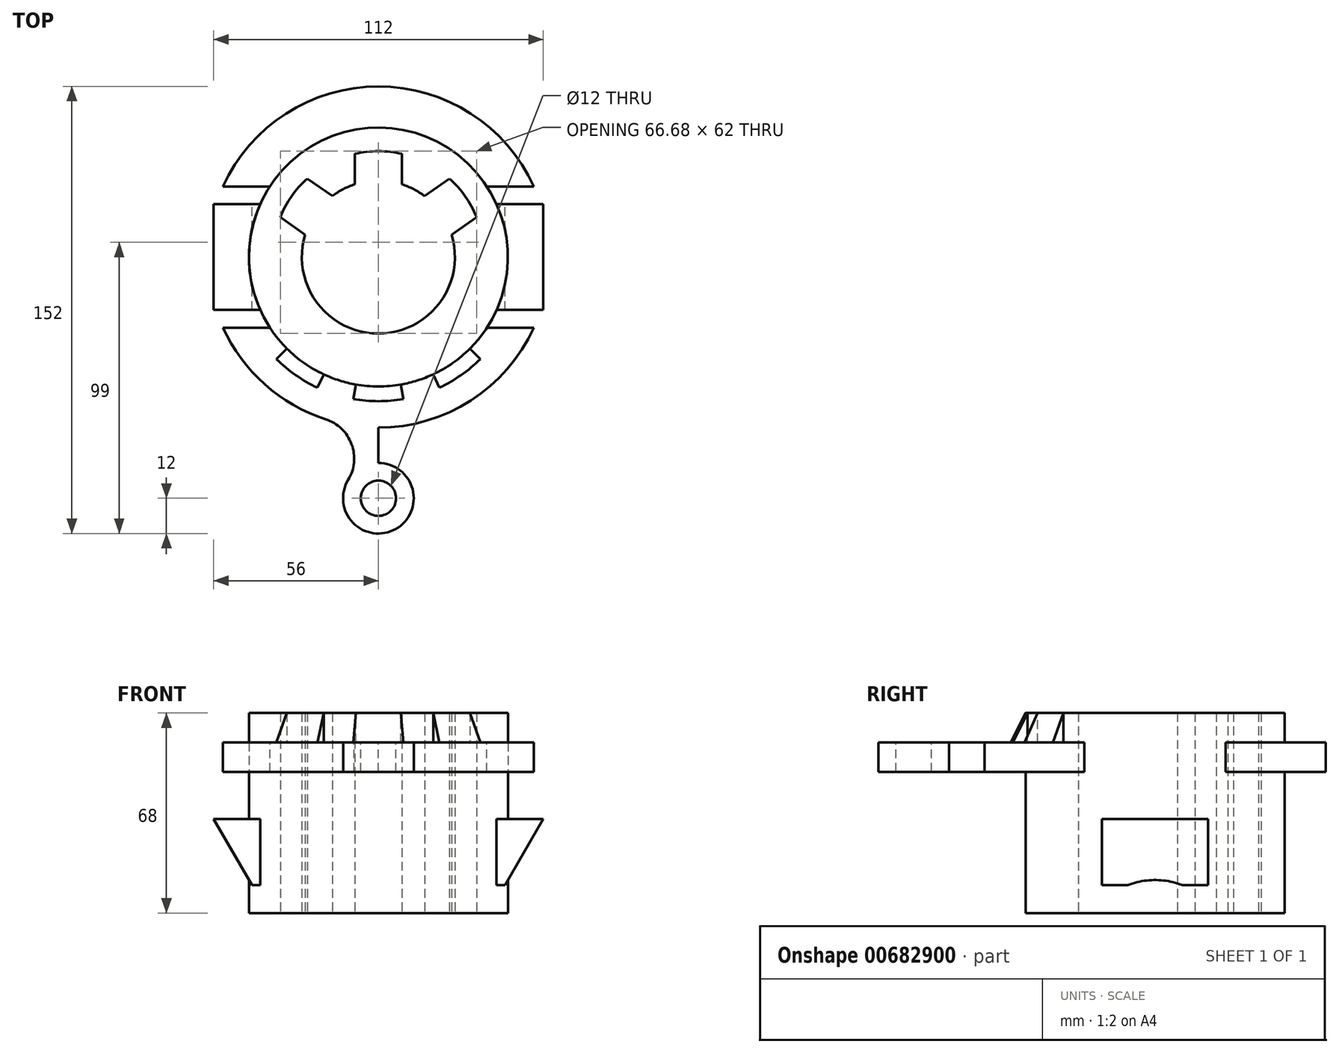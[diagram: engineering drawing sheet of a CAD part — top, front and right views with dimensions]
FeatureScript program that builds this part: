
annotation { "Feature Type Name" : "Feature", "Feature Type Description" : "" }
export const myFeature = defineFeature(function(context is Context, id is Id, definition is map)
    precondition{}
    {
        {
            var Q0;
            Q0=qCreatedBy(makeId("Top.planeOp"),FACE);
            var sketch = newSketch(context, id + "F0", { "sketchPlane" : qUnion([Q0])});
            skArc(sketch, "E0", {"start": v(-8, 24.74) * mm, "mid": v(-12, 23.06) * mm, "end": v(-15.68, 20.74) * mm});
            skCircle(sketch, "E1", {"center": v(0, 0) * mm, "radius": 44 * mm});
            skCircle(sketch, "E2", {"center": v(0, 0) * mm, "radius": 36 * mm});
            skLineSegment(sketch, "E3", {"start": v(0, 36) * mm, "end": v(0, 26) * mm});
            skLineSegment(sketch, "E4.0", {"start": v(8, 35.1) * mm, "end": v(8, 24.74) * mm});
            skLineSegment(sketch, "E5", {"start": v(0, 0) * mm, "end": v(41.6, 29.13) * mm});
            skLineSegment(sketch, "E6.MirrorCS", {"start": v(-8, 35.1) * mm, "end": v(-8, 24.74) * mm});
            skLineSegment(sketch, "E7", {"start": v(0, 0) * mm, "end": v(21.24, 40.8) * mm});
            skLineSegment(sketch, "E8.MirrorCS", {"start": v(24.16, 26.69) * mm, "end": v(15.68, 20.74) * mm});
            skLineSegment(sketch, "E9.MirrorCS", {"start": v(33.34, 13.58) * mm, "end": v(24.85, 7.64) * mm});
            skLineSegment(sketch, "E10.MirrorCS", {"start": v(-24.16, 26.69) * mm, "end": v(-15.68, 20.74) * mm});
            skLineSegment(sketch, "E11.MirrorCS", {"start": v(-33.34, 13.58) * mm, "end": v(-24.85, 7.64) * mm});
            skArc(sketch, "E12.trimOffspring", {"start": v(-24.85, 7.64) * mm, "mid": v(0, -26) * mm, "end": v(24.85, 7.64) * mm});
            skArc(sketch, "E13.trimOffspring", {"start": v(15.68, 20.74) * mm, "mid": v(12, 23.06) * mm, "end": v(8, 24.74) * mm});
            skSolve(sketch);
        }
        {
            var Q0;
            Q0=makeQuery(id+"F0.imprint","IMPRINT",FACE,{"disambiguationData":[TD([[makeQuery(id+"F0.imprint","IMPRINT",EDGE,{"derivedFrom":sQuery(id+"F0.wireOp",EDGE,"E0")}),-1.0]])]});
            var Q1;
            {var subQ0=sQuery(id+"F0.wireOp",EDGE,"E9.MirrorCS");Q1=makeQuery(id+"F0.imprint","IMPRINT",FACE,{"disambiguationData":[TD([[makeQuery(id+"F0.imprint","IMPRINT",EDGE,{"derivedFrom":subQ0}),1.0]])]});}
            var Q2;
            {var subQ0=sQuery(id+"F0.wireOp",EDGE,"E8.MirrorCS");Q2=makeQuery(id+"F0.imprint","IMPRINT",FACE,{"disambiguationData":[TD([[makeQuery(id+"F0.imprint","IMPRINT",EDGE,{"derivedFrom":subQ0}),-1.0]])]});}
            var Q3;
            {var subQ0=sQuery(id+"F0.wireOp",EDGE,"E4.0");Q3=makeQuery(id+"F0.imprint","IMPRINT",FACE,{"disambiguationData":[TD([[makeQuery(id+"F0.imprint","IMPRINT",EDGE,{"derivedFrom":subQ0}),1.0]])]});}
            var Q4;
            {var subQ0=sQuery(id+"F0.wireOp",EDGE,"E2");var subQ9=makeQuery(id+"F0.imprint","IMPRINT",VERTEX,{"derivedFrom":subQ0});Q4=makeQuery(id+"F0.imprint","IMPRINT",FACE,{"disambiguationData":[TD([[makeQuery(id+"F0.imprint","IMPRINT",EDGE,{"disambiguationData":[TD([[subQ9,1.0]])],"derivedFrom":subQ0}),-1.0]])]});}
            var Q5;
            {var subQ4=sQuery(id+"F0.wireOp",EDGE,"E5");var subQ5=sQuery(id+"F0.wireOp",EDGE,"E1");var subQ6=makeQuery(id+"F0.imprint","INTERSECT",VERTEX,{"derivedFrom":[subQ5,subQ4]});Q5=makeQuery(id+"F0.imprint","IMPRINT",FACE,{"disambiguationData":[TD([[makeQuery(id+"F0.imprint","IMPRINT",EDGE,{"disambiguationData":[TD([[subQ6,-1.0]])],"derivedFrom":subQ5}),1.0]])]});}
            extrude(context, id + "F1", {"entities" : qUnion([Q0, Q1, Q2, Q3, Q4, Q5]), "depth" : 68 * mm, "offsetDistance" : 25 * mm});
        }
        {
            var Q0;
            Q0=qCreatedBy(makeId("Right.planeOp"),FACE);
            var sketch = newSketch(context, id + "F2", { "sketchPlane" : qUnion([Q0])});
            skLineSegment(sketch, "E14", {"start": v(0, 0) * mm, "end": v(0, 68) * mm});
            skLineSegment(sketch, "E15", {"start": v(0, 68) * mm, "end": v(-44, 68) * mm});
            skLineSegment(sketch, "E16", {"start": v(-44, 68) * mm, "end": v(-44, 58) * mm});
            skLineSegment(sketch, "E17", {"start": v(-44, 58) * mm, "end": v(-49, 58) * mm});
            skLineSegment(sketch, "E18", {"start": v(-49, 58) * mm, "end": v(-44, 68) * mm});
            skSolve(sketch);
        }
        {
            var Q0;
            Q0=makeQuery(id+"F2.imprint","IMPRINT",FACE,{"disambiguationData":[TD([[makeQuery(id+"F2.imprint","IMPRINT",EDGE,{"derivedFrom":sQuery(id+"F2.wireOp",EDGE,"E16")}),-1.0]])]});
            var Q1;
            Q1=sQuery(id+"F2.wireOp",EDGE,"E14");
            revolve(context, id + "F3", {"operationType" : NewBodyOperationType.ADD, "entities" : qUnion([Q0]), "axis" : qUnion([Q1]), "revolveType" : RevolveType.SYMMETRIC, "angle" : 90 * degree});
        }
        {
            var Q0;
            Q0=makeQuery(id+"F1.opExtrude","CAP_FACE",FACE,{"disambiguationData":[OSD([sQuery(id+"F0.wireOp",EDGE,"E0"),sQuery(id+"F0.wireOp",EDGE,"E1"),sQuery(id+"F0.wireOp",EDGE,"E2"),sQuery(id+"F0.wireOp",EDGE,"E4.0"),sQuery(id+"F0.wireOp",EDGE,"E6.MirrorCS"),sQuery(id+"F0.wireOp",EDGE,"E8.MirrorCS"),sQuery(id+"F0.wireOp",EDGE,"E9.MirrorCS"),sQuery(id+"F0.wireOp",EDGE,"E10.MirrorCS"),sQuery(id+"F0.wireOp",EDGE,"E11.MirrorCS"),sQuery(id+"F0.wireOp",EDGE,"E12.trimOffspring"),sQuery(id+"F0.wireOp",EDGE,"E13.trimOffspring")])],"isStart":false});
            var sketch = newSketch(context, id + "F4", { "sketchPlane" : qUnion([Q0])});
            skLineSegment(sketch, "E19", {"start": v(0, 0) * mm, "end": v(0, -49) * mm});
            skLineSegment(sketch, "E20", {"start": v(0, 0) * mm, "end": v(-28.1, -40.14) * mm});
            skLineSegment(sketch, "E21", {"start": v(0, 0) * mm, "end": v(-34.65, -34.65) * mm});
            skCircle(sketch, "E22", {"center": v(0, 0) * mm, "radius": 44 * mm});
            skLineSegment(sketch, "E23", {"start": v(0, 0) * mm, "end": v(-8.5, -48.26) * mm});
            skLineSegment(sketch, "E24", {"start": v(0, 0) * mm, "end": v(8.5, -48.26) * mm});
            skLineSegment(sketch, "E25", {"start": v(0, 0) * mm, "end": v(20.7, -44.4) * mm});
            skCircle(sketch, "E26", {"center": v(0, 0) * mm, "radius": 49 * mm});
            skLineSegment(sketch, "E27.MirrorCS", {"start": v(0, 0) * mm, "end": v(-20.7, -44.4) * mm});
            skSolve(sketch);
        }
        {
            var Q0;
            {var subQ0=sQuery(id+"F4.wireOp",EDGE,"E27.MirrorCS");var subQ1=sQuery(id+"F4.wireOp",EDGE,"E22");var subQ2=makeQuery(id+"F4.imprint","INTERSECT",VERTEX,{"derivedFrom":[subQ1,subQ0]});Q0=makeQuery(id+"F4.imprint","IMPRINT",FACE,{"disambiguationData":[TD([[makeQuery(id+"F4.imprint","IMPRINT",EDGE,{"disambiguationData":[TD([[subQ2,-1.0]])],"derivedFrom":subQ1}),-1.0]])]});}
            var Q1;
            {var subQ0=sQuery(id+"F4.wireOp",EDGE,"E24");var subQ1=sQuery(id+"F4.wireOp",EDGE,"E22");var subQ2=makeQuery(id+"F4.imprint","INTERSECT",VERTEX,{"derivedFrom":[subQ1,subQ0]});Q1=makeQuery(id+"F4.imprint","IMPRINT",FACE,{"disambiguationData":[TD([[makeQuery(id+"F4.imprint","IMPRINT",EDGE,{"disambiguationData":[TD([[subQ2,-1.0]])],"derivedFrom":subQ1}),-1.0]])]});}
            var Q2;
            Q2=makeQuery(id+"F3.opRevolve","SWEPT_FACE",FACE,{"disambiguationData":[OSD([sQuery(id+"F2.wireOp",EDGE,"E17")])]});
            extrude(context, id + "F5", {"entities" : qUnion([Q0, Q1]), "operationType" : NewBodyOperationType.REMOVE, "endBound" : BoundingType.UP_TO_SURFACE, "oppositeDirection" : true, "depth" : 25 * mm, "endBoundEntityFace" : qUnion([Q2]), "offsetDistance" : 25 * mm});
        }
        {
            var Q0;
            {var subQ2=sQuery(id+"F4.wireOp",EDGE,"E23");Q0=makeQuery(id+"F5.boolean.opBoolean","SPLIT",FACE,{"disambiguationData":[TD([makeQuery(id+"F5.opExtrude","SWEPT_FACE",FACE,{"disambiguationData":[OSD([subQ2])]})])],"derivedFrom":makeQuery(id+"F3.opRevolve","SWEPT_FACE",FACE,{"disambiguationData":[OSD([sQuery(id+"F2.wireOp",EDGE,"E17")])]})});}
            var sketch = newSketch(context, id + "F6", { "sketchPlane" : qUnion([Q0])});
            skCircle(sketch, "E28", {"center": v(0, 0) * mm, "radius": 44 * mm});
            skArc(sketch, "E29", {"start": v(-52.8, -24) * mm, "mid": v(0, -58) * mm, "end": v(52.8, -24) * mm});
            skLineSegment(sketch, "E30", {"start": v(-58, 0) * mm, "end": v(58, 0) * mm});
            skLineSegment(sketch, "E31.0", {"start": v(-58, -24) * mm, "end": v(58, -24) * mm});
            skLineSegment(sketch, "E32.MirrorCS", {"start": v(-58, 24) * mm, "end": v(58, 24) * mm});
            skArc(sketch, "E33.trimOffspring", {"start": v(52.8, 24) * mm, "mid": v(0, 58) * mm, "end": v(-52.8, 24) * mm});
            skLineSegment(sketch, "E34", {"start": v(0, 0) * mm, "end": v(0, 82) * mm});
            skCircle(sketch, "E35", {"center": v(0, 82) * mm, "radius": 6 * mm});
            skCircle(sketch, "E36", {"center": v(0, 82) * mm, "radius": 12 * mm});
            skArc(sketch, "E37", {"start": v(-17.9, 55.17) * mm, "mid": v(-9.09, 63.62) * mm, "end": v(-10.25, 75.76) * mm});
            skArc(sketch, "E38.MirrorCS", {"start": v(17.9, 55.17) * mm, "mid": v(9.09, 63.62) * mm, "end": v(10.25, 75.76) * mm});
            skSolve(sketch);
        }
        {
            var Q0;
            {var subQ0=sQuery(id+"F6.wireOp",EDGE,"E33.trimOffspring");Q0=makeQuery(id+"F6.imprint","IMPRINT",FACE,{"disambiguationData":[TD([[makeQuery(id+"F6.imprint","IMPRINT",EDGE,{"derivedFrom":subQ0}),1.0]])]});}
            var Q1;
            {var subQ4=sQuery(id+"F6.wireOp",EDGE,"E29");Q1=makeQuery(id+"F6.imprint","IMPRINT",FACE,{"disambiguationData":[TD([[makeQuery(id+"F6.imprint","IMPRINT",EDGE,{"derivedFrom":subQ4}),1.0]])]});}
            var Q2;
            {var subQ1=sQuery(id+"F4.wireOp",EDGE,"E23");var subQ2=makeQuery(id+"F5.boolean.opBoolean","COPY",EDGE,{"derivedFrom":makeQuery(id+"F5.opExtrude","CAP_EDGE",EDGE,{"disambiguationData":[OSD([subQ1])],"isStart":false})});Q2=makeQuery(id+"F6.imprint","IMPRINT",FACE,{"disambiguationData":[TD([[makeQuery(id+"F6.imprint","IMPRINT",EDGE,{"derivedFrom":subQ2}),-1.0]])]});}
            var Q3;
            {var subQ1=sQuery(id+"F4.wireOp",EDGE,"E24");var subQ2=makeQuery(id+"F5.boolean.opBoolean","COPY",EDGE,{"derivedFrom":makeQuery(id+"F5.opExtrude","CAP_EDGE",EDGE,{"disambiguationData":[OSD([subQ1])],"isStart":false})});Q3=makeQuery(id+"F6.imprint","IMPRINT",FACE,{"disambiguationData":[TD([[makeQuery(id+"F6.imprint","IMPRINT",EDGE,{"derivedFrom":subQ2}),1.0]])]});}
            var Q4;
            {var subQ0=sQuery(id+"F6.wireOp",EDGE,"E38.MirrorCS");Q4=makeQuery(id+"F6.imprint","IMPRINT",FACE,{"disambiguationData":[TD([[makeQuery(id+"F6.imprint","IMPRINT",EDGE,{"derivedFrom":subQ0}),1.0]])]});}
            var Q5;
            {var subQ0=sQuery(id+"F6.wireOp",EDGE,"E37");Q5=makeQuery(id+"F6.imprint","IMPRINT",FACE,{"disambiguationData":[TD([[makeQuery(id+"F6.imprint","IMPRINT",EDGE,{"derivedFrom":subQ0}),-1.0]])]});}
            var Q6;
            Q6=makeQuery(id+"F6.imprint","IMPRINT",FACE,{"disambiguationData":[TD([[makeQuery(id+"F6.imprint","IMPRINT",EDGE,{"derivedFrom":sQuery(id+"F6.wireOp",EDGE,"E35")}),-1.0]])]});
            extrude(context, id + "F7", {"entities" : qUnion([Q0, Q1, Q2, Q3, Q4, Q5, Q6]), "operationType" : NewBodyOperationType.ADD, "depth" : 10 * mm, "offsetDistance" : 25 * mm});
        }
        {
            var Q0;
            Q0=qCreatedBy(makeId("Front.planeOp"),FACE);
            var sketch = newSketch(context, id + "F8", { "sketchPlane" : qUnion([Q0])});
            skLineSegment(sketch, "E39", {"start": v(0, 0) * mm, "end": v(44, 0) * mm});
            skLineSegment(sketch, "E40", {"start": v(44, 0) * mm, "end": v(44, 32) * mm});
            skLineSegment(sketch, "E41", {"start": v(44, 32) * mm, "end": v(56, 32) * mm});
            skLineSegment(sketch, "E42", {"start": v(56, 32) * mm, "end": v(43, 9.48) * mm});
            skLineSegment(sketch, "E43", {"start": v(56, 32) * mm, "end": v(66.19, 32) * mm});
            skLineSegment(sketch, "E44", {"start": v(44, 32) * mm, "end": v(43, 32) * mm});
            skLineSegment(sketch, "E45", {"start": v(43, 32) * mm, "end": v(43, 9.48) * mm});
            skSolve(sketch);
        }
        {
            var Q0;
            {var subQ0=sQuery(id+"F8.wireOp",EDGE,"E44");Q0=makeQuery(id+"F8.imprint","IMPRINT",FACE,{"disambiguationData":[TD([[makeQuery(id+"F8.imprint","IMPRINT",EDGE,{"derivedFrom":subQ0}),1.0]])]});}
            var Q1;
            {var subQ0=sQuery(id+"F8.wireOp",EDGE,"E41");Q1=makeQuery(id+"F8.imprint","IMPRINT",FACE,{"disambiguationData":[TD([[makeQuery(id+"F8.imprint","IMPRINT",EDGE,{"derivedFrom":subQ0}),-1.0]])]});}
            extrude(context, id + "F9", {"entities" : qUnion([Q0, Q1]), "operationType" : NewBodyOperationType.ADD, "endBound" : BoundingType.SYMMETRIC, "depth" : 36 * mm, "offsetDistance" : 25 * mm});
        }
        {
            var Q0;
            {var subQ0=sQuery(id+"F8.wireOp",EDGE,"E45");var subQ1=sQuery(id+"F8.wireOp",EDGE,"E44");var subQ2=sQuery(id+"F8.wireOp",EDGE,"E42");var subQ3=sQuery(id+"F8.wireOp",EDGE,"E41");Q0=makeQuery(id+"F9.boolean.opBoolean","SPLIT",FACE,{"disambiguationData":[TD([makeQuery(id+"F9.opExtrude","CAP_FACE",FACE,{"disambiguationData":[OSD([subQ3,subQ2,subQ1,subQ0])],"isStart":true})])],"derivedFrom":makeQuery(id+"F9.opExtrude","SWEPT_FACE",FACE,{"disambiguationData":[OSD([subQ0])]})});}
            var Q1;
            {var subQ0=sQuery(id+"F8.wireOp",EDGE,"E45");var subQ1=sQuery(id+"F8.wireOp",EDGE,"E44");var subQ2=sQuery(id+"F8.wireOp",EDGE,"E42");var subQ3=sQuery(id+"F8.wireOp",EDGE,"E41");Q1=makeQuery(id+"F9.boolean.opBoolean","SPLIT",FACE,{"disambiguationData":[TD([makeQuery(id+"F9.opExtrude","CAP_FACE",FACE,{"disambiguationData":[OSD([subQ3,subQ2,subQ1,subQ0])],"isStart":false})])],"derivedFrom":makeQuery(id+"F9.opExtrude","SWEPT_FACE",FACE,{"disambiguationData":[OSD([subQ0])]})});}
            var Q2;
            {var subQ0=sQuery(id+"F6.wireOp",EDGE,"E31.0");var subQ1=sQuery(id+"F6.wireOp",EDGE,"E29");var subQ19=sQuery(id+"F0.wireOp",EDGE,"E1");var subQ23=sQuery(id+"F4.wireOp",EDGE,"E22");Q2=makeQuery(id+"F7.boolean.opBoolean","SPLIT",FACE,{"disambiguationData":[TD([makeQuery(id+"F7.opExtrude","SWEPT_FACE",FACE,{"disambiguationData":[OSD([subQ0]),TDD([makeQuery(id+"F6.imprint","IMPRINT",EDGE,{"disambiguationData":[TD([[makeQuery(id+"F6.imprint","INTERSECT",VERTEX,{"disambiguationData":[OD(0.0)],"derivedFrom":[subQ1,subQ0]}),-1.0]])],"derivedFrom":subQ0})])]})])],"derivedFrom":makeQuery(id+"F5.boolean.opBoolean","MERGE",FACE,{"derivedFrom":[makeQuery(id+"F1.opExtrude","SWEPT_FACE",FACE,{"disambiguationData":[OSD([subQ19])]})],"fromTools":[makeQuery(id+"F5.opExtrude","SWEPT_FACE",FACE,{"disambiguationData":[OSD([subQ23]),TDD([makeQuery(id+"F4.imprint","IMPRINT",EDGE,{"disambiguationData":[TD([[makeQuery(id+"F4.imprint","INTERSECT",VERTEX,{"derivedFrom":[subQ23,sQuery(id+"F4.wireOp",EDGE,"E27.MirrorCS")]}),-1.0]])],"derivedFrom":subQ23})])]}),makeQuery(id+"F5.opExtrude","SWEPT_FACE",FACE,{"disambiguationData":[OSD([subQ23]),TDD([makeQuery(id+"F4.imprint","IMPRINT",EDGE,{"disambiguationData":[TD([[makeQuery(id+"F4.imprint","INTERSECT",VERTEX,{"derivedFrom":[subQ23,sQuery(id+"F4.wireOp",EDGE,"E24")]}),-1.0]])],"derivedFrom":subQ23})])]})]})});}
            extrude(context, id + "F10", {"entities" : qUnion([Q0, Q1]), "operationType" : NewBodyOperationType.ADD, "endBound" : BoundingType.UP_TO_SURFACE, "depth" : 25 * mm, "endBoundEntityFace" : qUnion([Q2]), "offsetDistance" : 25 * mm});
        }
        {
            var Q0;
            Q0=qCreatedBy(makeId("Front.planeOp"),FACE);
            var sketch = newSketch(context, id + "F11", { "sketchPlane" : qUnion([Q0])});
            skLineSegment(sketch, "E46", {"start": v(0, 0) * mm, "end": v(-44, 0) * mm});
            skLineSegment(sketch, "E47", {"start": v(-44, 0) * mm, "end": v(-44, 32) * mm});
            skLineSegment(sketch, "E48", {"start": v(-44, 32) * mm, "end": v(-56, 32) * mm});
            skLineSegment(sketch, "E49", {"start": v(-44, 32) * mm, "end": v(-43, 32) * mm});
            skLineSegment(sketch, "E50", {"start": v(-56, 32) * mm, "end": v(-43, 9.48) * mm});
            skLineSegment(sketch, "E51", {"start": v(-43, 32) * mm, "end": v(-43, 9.48) * mm});
            skSolve(sketch);
        }
        {
            var Q0;
            {var subQ0=sQuery(id+"F11.wireOp",EDGE,"E48");Q0=makeQuery(id+"F11.imprint","IMPRINT",FACE,{"disambiguationData":[TD([[makeQuery(id+"F11.imprint","IMPRINT",EDGE,{"derivedFrom":subQ0}),1.0]])]});}
            var Q1;
            {var subQ0=sQuery(id+"F11.wireOp",EDGE,"E49");Q1=makeQuery(id+"F11.imprint","IMPRINT",FACE,{"disambiguationData":[TD([[makeQuery(id+"F11.imprint","IMPRINT",EDGE,{"derivedFrom":subQ0}),-1.0]])]});}
            extrude(context, id + "F12", {"entities" : qUnion([Q0, Q1]), "operationType" : NewBodyOperationType.ADD, "endBound" : BoundingType.SYMMETRIC, "depth" : 36 * mm, "offsetDistance" : 25 * mm});
        }
        {
            var Q0;
            {var subQ0=sQuery(id+"F11.wireOp",EDGE,"E49");var subQ1=sQuery(id+"F11.wireOp",EDGE,"E48");var subQ3=sQuery(id+"F11.wireOp",EDGE,"E51");var subQ4=sQuery(id+"F11.wireOp",EDGE,"E50");Q0=makeQuery(id+"F12.boolean.opBoolean","SPLIT",FACE,{"disambiguationData":[TD([makeQuery(id+"F12.opExtrude","CAP_FACE",FACE,{"disambiguationData":[OSD([subQ1,subQ0,subQ4,subQ3])],"isStart":false})])],"derivedFrom":makeQuery(id+"F12.opExtrude","SWEPT_FACE",FACE,{"disambiguationData":[OSD([subQ3])]})});}
            var Q1;
            {var subQ0=sQuery(id+"F11.wireOp",EDGE,"E49");var subQ1=sQuery(id+"F11.wireOp",EDGE,"E48");var subQ3=sQuery(id+"F11.wireOp",EDGE,"E51");var subQ4=sQuery(id+"F11.wireOp",EDGE,"E50");Q1=makeQuery(id+"F12.boolean.opBoolean","SPLIT",FACE,{"disambiguationData":[TD([makeQuery(id+"F12.opExtrude","CAP_FACE",FACE,{"disambiguationData":[OSD([subQ1,subQ0,subQ4,subQ3])],"isStart":true})])],"derivedFrom":makeQuery(id+"F12.opExtrude","SWEPT_FACE",FACE,{"disambiguationData":[OSD([subQ3])]})});}
            var Q2;
            {var subQ0=sQuery(id+"F6.wireOp",EDGE,"E31.0");var subQ1=sQuery(id+"F6.wireOp",EDGE,"E29");var subQ19=sQuery(id+"F0.wireOp",EDGE,"E1");var subQ23=sQuery(id+"F4.wireOp",EDGE,"E22");Q2=makeQuery(id+"F7.boolean.opBoolean","SPLIT",FACE,{"disambiguationData":[TD([makeQuery(id+"F7.opExtrude","SWEPT_FACE",FACE,{"disambiguationData":[OSD([subQ0]),TDD([makeQuery(id+"F6.imprint","IMPRINT",EDGE,{"disambiguationData":[TD([[makeQuery(id+"F6.imprint","INTERSECT",VERTEX,{"disambiguationData":[OD(0.0)],"derivedFrom":[subQ1,subQ0]}),-1.0]])],"derivedFrom":subQ0})])]})])],"derivedFrom":makeQuery(id+"F5.boolean.opBoolean","MERGE",FACE,{"derivedFrom":[makeQuery(id+"F1.opExtrude","SWEPT_FACE",FACE,{"disambiguationData":[OSD([subQ19])]})],"fromTools":[makeQuery(id+"F5.opExtrude","SWEPT_FACE",FACE,{"disambiguationData":[OSD([subQ23]),TDD([makeQuery(id+"F4.imprint","IMPRINT",EDGE,{"disambiguationData":[TD([[makeQuery(id+"F4.imprint","INTERSECT",VERTEX,{"derivedFrom":[subQ23,sQuery(id+"F4.wireOp",EDGE,"E27.MirrorCS")]}),-1.0]])],"derivedFrom":subQ23})])]}),makeQuery(id+"F5.opExtrude","SWEPT_FACE",FACE,{"disambiguationData":[OSD([subQ23]),TDD([makeQuery(id+"F4.imprint","IMPRINT",EDGE,{"disambiguationData":[TD([[makeQuery(id+"F4.imprint","INTERSECT",VERTEX,{"derivedFrom":[subQ23,sQuery(id+"F4.wireOp",EDGE,"E24")]}),-1.0]])],"derivedFrom":subQ23})])]})]})});}
            extrude(context, id + "F13", {"entities" : qUnion([Q0, Q1]), "operationType" : NewBodyOperationType.ADD, "endBound" : BoundingType.UP_TO_SURFACE, "depth" : 25 * mm, "endBoundEntityFace" : qUnion([Q2]), "offsetDistance" : 25 * mm});
        }
    });
